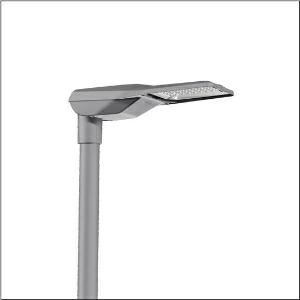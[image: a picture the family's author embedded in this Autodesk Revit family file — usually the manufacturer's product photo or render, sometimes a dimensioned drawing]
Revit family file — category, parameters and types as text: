
# Revit family: streetlight_sl_21_iq_mini___stw1_0a_5xe2e41g08hb_6f26
name_source: partatom
category: Lighting Fixtures
units: mm (PartAtom-declared; Revit-internal decimal feet)

## family parameters
Cut with Voids When Loaded = No
Host = Face
Light Source = No
Part Type = Normal
Room Calculation Point = No
Round Connector Dimension = Use Diameter
Shared = No

## types (1)
- --- (1 x LED, 9860 lm, 70.9 W, 4000K)
    Apparent Load = 71 VA
    CIE Flux Codes = 38 75 98 100 100
    Color Rendering = 70
    Color Temperature = 4000K
    Default Elevation = 1800 mm
    Description = Streetlight SL 21 iQ mini, mast luminaire, primary light control with lens, of PMMA, primary optical cover: cover, of toughened safety glass, transparent, light distribution: STW1.0a, light emission: direct distribution, primary light characteristic: asymmetric, installation type: post-top, side-entry, LED, High Power LED, rated luminous flux: 9.860lm, luminous efficacy: 139lm/W, light colour: 740, colour temperature: 4000K, control: Street-Remote, Auto-Match, Temp-Guard, Lumen-Switch, Night-Set, Smart-Wire, Light-Fading, Desk-Remote (wireless, voltage-free reading and setting of iQ features in the workshop via application-optimized NFC function/RFID function), optimised constant luminous flux control (CLO 2.0), presetting dimming linear, mains connection: 220..240V, AC, 50/60Hz, start of lifetime: 71W, end of service life: 75W, reduction: 31W, luminaire housing, of diecast aluminium, powder-coated, Siteco® metallic grey (DB 702S), corrosivity category C5 mid according to DIN EN ISO 12944, please order mast flange separately, inclination adjustable: 0°, 5°, 10°, 15°, sealing non-destructively replaceable, multi-level sealing system, length: 628mm, width: 235mm, height: 110mm, mast flange for spigot size: 42mm (side-entry): 5XC10008XM4, 60/48mm (side-entry/post-top): 5XC10108XM2, 76/60mm (side-entry/post-top): 5XC10108XM1, protection rating (complete): IP66, insulation class (complete): insulation class II (safety insulation), certification: CE, ENEC, ENEC+, VDE, impact resistance: IK09, permissible operating ambient temperature for outdoor applications: -40..+50°C, standard-compliant lighting for roads and squares, packaging unit: 1 piece

Light Distribution: STW1.0a
    Height = 110 mm
    Lamp = 1 x LED
    Lamp Light Flux = 9860 lm
    Lamp Power = 70.9 W
    Lamp count = 1
    Length = 625 mm
    Luminous efficacy = 139 lm/W
    Manufacturer = Siteco
    ModVariant = No
    Model = 5XE2E41G08HB
    Number of Poles = 1
    OnlyDefault = Yes
    Power Factor = 1
    Product Name = Streetlight SL 21 iQ mini | STW1.0a
    Product group = mast luminaire | pylon top
    ProductGroupID = 6100
    Protection Class = Protection class II
    Protection Degree = IP 66
    RLX_Detail_Level = 1
    RLX_Emergency_Light_Flux = 0 lm
    RLX_Emergency_Type = 0
    RLX_Emergency_Type_DB = No
    RlxData = <blob elided: 92417 chars, md5=95334449>
    Socket = socket
    Standby Power = 0 W
    System Light Flux = 9860 lm
    System Power = 71 W
    Type Comments = factory setting: luminous flux: 100 % | dim-lin: 254 | 711 mA
    Type Image = l_1003519.jpg
    URL = http://relux.com
    VarID = @adj_090077
    Voltage = 0 V
    Weight = 0.00 kg
    Width = 234 mm

## geometry (parser evidence)
native form markers: Blend x4, Sweep x12
no freeform markers — native parametric forms only
